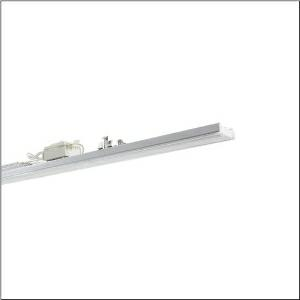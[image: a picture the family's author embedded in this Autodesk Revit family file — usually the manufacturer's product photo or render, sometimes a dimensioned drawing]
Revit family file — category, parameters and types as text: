
# Revit family: licross_11_recessed_ho_51te12dv4m2m3s4
name_source: partatom
category: Lighting Fixtures
units: mm (PartAtom-declared; Revit-internal decimal feet)

## family parameters
Cut with Voids When Loaded = No
Host = Face
Light Source = No
Part Type = Normal
Room Calculation Point = No
Round Connector Dimension = Use Diameter
Shared = No

## types (1)
- --- (1 x LED, 1010 lm, 5.9 W, 4000K)
    Apparent Load = 6 VA
    CIE Flux Codes = 66 91 98 100 100
    Color Rendering = 80
    Color Temperature = 4000K
    Default Elevation = 1800 mm
    Description = Licross 11 Recessed HO, luminaire insert, of sheet steel, galvanised, coil coated, white, length: 2.250mm, width: 66mm, height: 67mm, LED rated luminous flux: 27.150lm, light colour: 840, SDCM (Standard Deviation of Colour Matching)MacAdam ≤ 2 SDCM (initial), control gear: DALI 2, with plug, 6-pole, with phase selection, for trunking rail, 9 or 11-core, mains connection: 220..240V, AC, 50/60Hz, rated input power: 154W, for trunking rail, 9-/11-core, internal wiring halogen-free, for emergency light function, converter,control gear: single battery element, battery: LiFePO4, 9Ah, primary optical cover: cover, of PMMA, light emission: direct distribution, primary light characteristic: symmetric, protection rating (complete): IP54, insulation class (complete): insulation class I (protective earthing), certification: CE, UKCA, protection symbol: D if used in an environment with non-conductive dust loads with corresponding accessories, impact resistance: IK06, permissible ambient temperature for indoor applications: +5..+35°C, standard: EN 60598-2-22, LABS conformity tested according to VDMA 24364:2018-05, reducing of maximum allowable ambient temperature of 5°C with ceiling mounting, corresponds to IFS (International Featured Standards) requirements for safety and quality in the food industry, The light source and the operating device comply with the requirements of the Ecodesign Regulation (EU) 2019/2020 and are replaceable in accordance with this regulation, packaging unit: 1 piece
    Height = 58 mm
    Lamp = 1 x LED
    Lamp Light Flux = 1010 lm
    Lamp Power = 5.9 W
    Lamp count = 1
    Length = 2250 mm
    Luminous efficacy = 171 lm/W
    Manufacturer = Siteco
    ModVariant = No
    Model = 51TE12DV4M2M3S4
    Mounting Place = Ceiling
    Mounting Type = Pendant
    Number of Poles = 1
    OnlyDefault = Yes
    Power Factor = 1
    Product Name = Licross 11 Recessed HO
    Product group = luminaire insert | ceiling pendant
    ProductGroupID = 901
    Protection Class = Protection class I
    Protection Degree = IP 54
    RLX_Detail_Level = 1
    RLX_Emergency_Light_Flux = 0 lm
    RLX_Emergency_Type = 0
    RLX_Emergency_Type_DB = No
    RlxData = <blob elided: 30069 chars, md5=4d369b42>
    Socket = socket
    Standby Power = 0 W
    System Light Flux = 1010 lm
    System Power = 6 W
    Type Comments = : emergency light operation: 3 h
    Type Image = l_1296930.jpg
    URL = http://relux.com
    VarID = @adj_089615
    Voltage = 0 V
    Weight = 0.00 kg
    Width = 66 mm

## geometry (parser evidence)
native form markers: Blend x4, Sweep x10
no freeform markers — native parametric forms only
